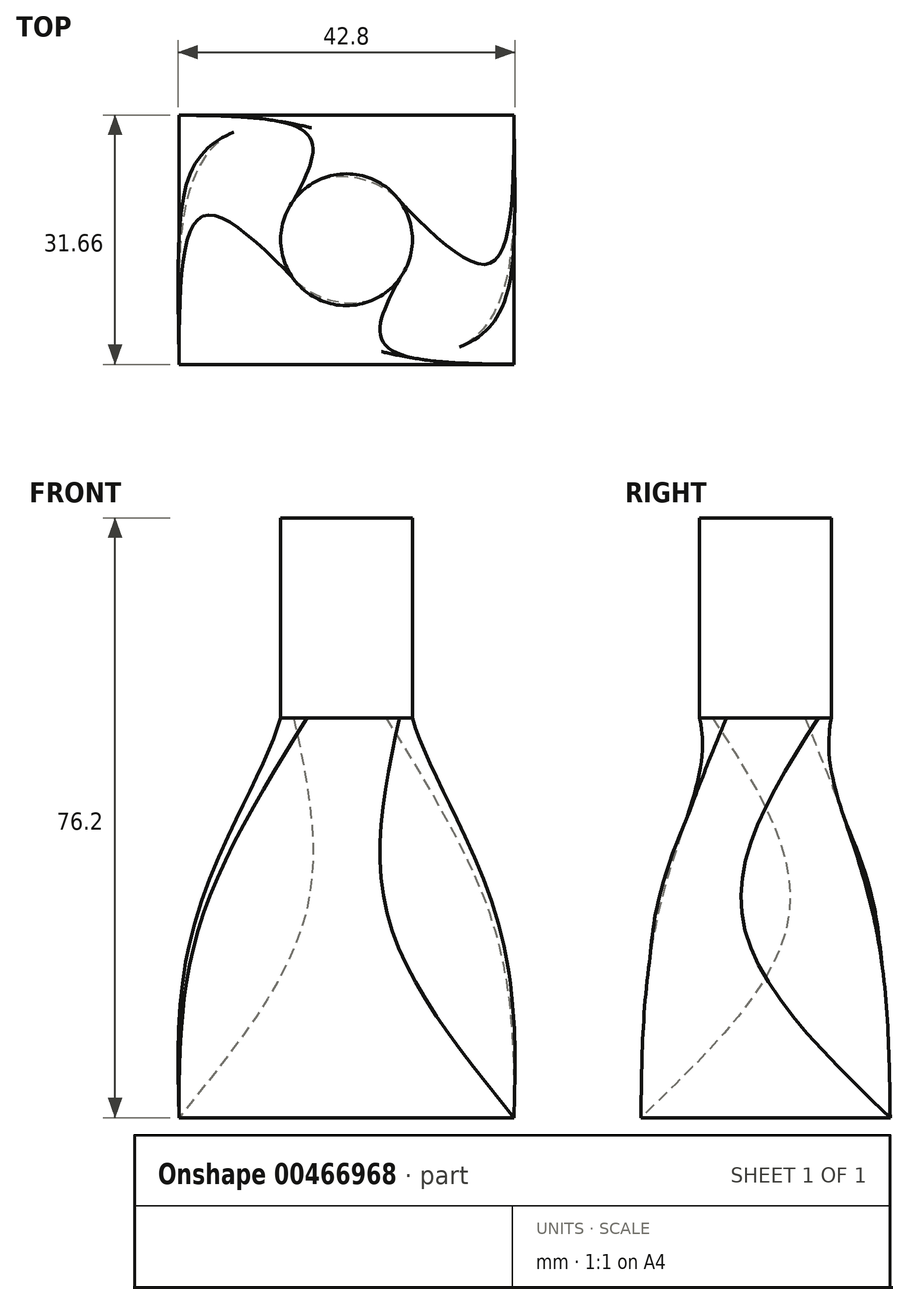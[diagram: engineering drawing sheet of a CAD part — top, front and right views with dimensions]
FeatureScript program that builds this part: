
annotation { "Feature Type Name" : "Feature", "Feature Type Description" : "" }
export const myFeature = defineFeature(function(context is Context, id is Id, definition is map)
    precondition{}
    {
        {
            var Q0;
            Q0=qCreatedBy(makeId("Top.planeOp"),FACE);
            var sketch = newSketch(context, id + "F0", { "sketchPlane" : qUnion([Q0])});
            skLineSegment(sketch, "E0.bottom", {"start": v(21.3, -15.83) * mm, "end": v(-21.3, -15.83) * mm});
            skLineSegment(sketch, "E0.top", {"start": v(21.3, 15.83) * mm, "end": v(-21.3, 15.83) * mm});
            skLineSegment(sketch, "E0.left", {"start": v(21.3, -15.83) * mm, "end": v(21.3, 15.83) * mm});
            skLineSegment(sketch, "E0.right", {"start": v(-21.3, -15.83) * mm, "end": v(-21.3, 15.83) * mm});
            skPoint(sketch, "E0.middle", {"position": v(0, 0) * mm});
            skSolve(sketch);
        }
        {
            var Q0;
            Q0=qCreatedBy(makeId("Top.planeOp"),FACE);
            cPlane(context, id + "F1", {"entities" : qUnion([Q0]), "cplaneType" : CPlaneType.OFFSET, "offset" : 25.4 * mm, "width" : 152.4 * mm, "height" : 152.4 * mm});
        }
        {
            var Q0;
            Q0=qCreatedBy(id+"F1.planeOp",FACE);
            var sketch = newSketch(context, id + "F2", { "sketchPlane" : qUnion([Q0])});
            skEllipse(sketch, "E1", {"center": v(0, 0) * mm, "majorRadius": 20.82 * mm, "minorRadius": 11.37 * mm, "majorAxis": v(0.88, -0.47)});
            skSolve(sketch);
        }
        {
            var Q0;
            Q0=qCreatedBy(id+"F1.planeOp",FACE);
            cPlane(context, id + "F3", {"entities" : qUnion([Q0]), "cplaneType" : CPlaneType.OFFSET, "offset" : 25.4 * mm, "width" : 152.4 * mm, "height" : 152.4 * mm});
        }
        {
            var Q0;
            Q0=qCreatedBy(id+"F3.planeOp",FACE);
            var sketch = newSketch(context, id + "F4", { "sketchPlane" : qUnion([Q0])});
            skCircle(sketch, "E2", {"center": v(0, 0) * mm, "radius": 8.37 * mm});
            skSolve(sketch);
        }
        {
            var Q0;
            Q0=makeQuery(id+"F4.imprint","IMPRINT",FACE,{"disambiguationData":[TD([[makeQuery(id+"F4.imprint","IMPRINT",EDGE,{"derivedFrom":sQuery(id+"F4.wireOp",EDGE,"E2")}),1.0]])]});
            var Q1;
            Q1=makeQuery(id+"F2.imprint","IMPRINT",FACE,{"disambiguationData":[TD([[makeQuery(id+"F2.imprint","IMPRINT",EDGE,{"derivedFrom":sQuery(id+"F2.wireOp",EDGE,"E1")}),1.0]])]});
            var Q2;
            Q2=makeQuery(id+"F0.imprint","IMPRINT",FACE,{"disambiguationData":[TD([[makeQuery(id+"F0.imprint","IMPRINT",EDGE,{"derivedFrom":sQuery(id+"F0.wireOp",EDGE,"E0.bottom")}),-1.0]])]});
            loft(context, id + "F5", {"sheetProfilesArray" : [{ "sheetProfileEntities" : qUnion([Q0]) }, { "sheetProfileEntities" : qUnion([Q1]) }, { "sheetProfileEntities" : qUnion([Q2]) }]});
        }
        {
            var Q0;
            Q0=makeQuery(id+"F5.opLoft","CAP_FACE",FACE,{"disambiguationData":[OSD([makeQuery(id+"F4.imprint","IMPRINT",FACE,{"disambiguationData":[TD([[makeQuery(id+"F4.imprint","IMPRINT",EDGE,{"derivedFrom":sQuery(id+"F4.wireOp",EDGE,"E2")}),1.0]])]})])],"isStart":true});
            extrude(context, id + "F6", {"entities" : qUnion([Q0]), "operationType" : NewBodyOperationType.ADD, "depth" : 25.4 * mm});
        }
    });
